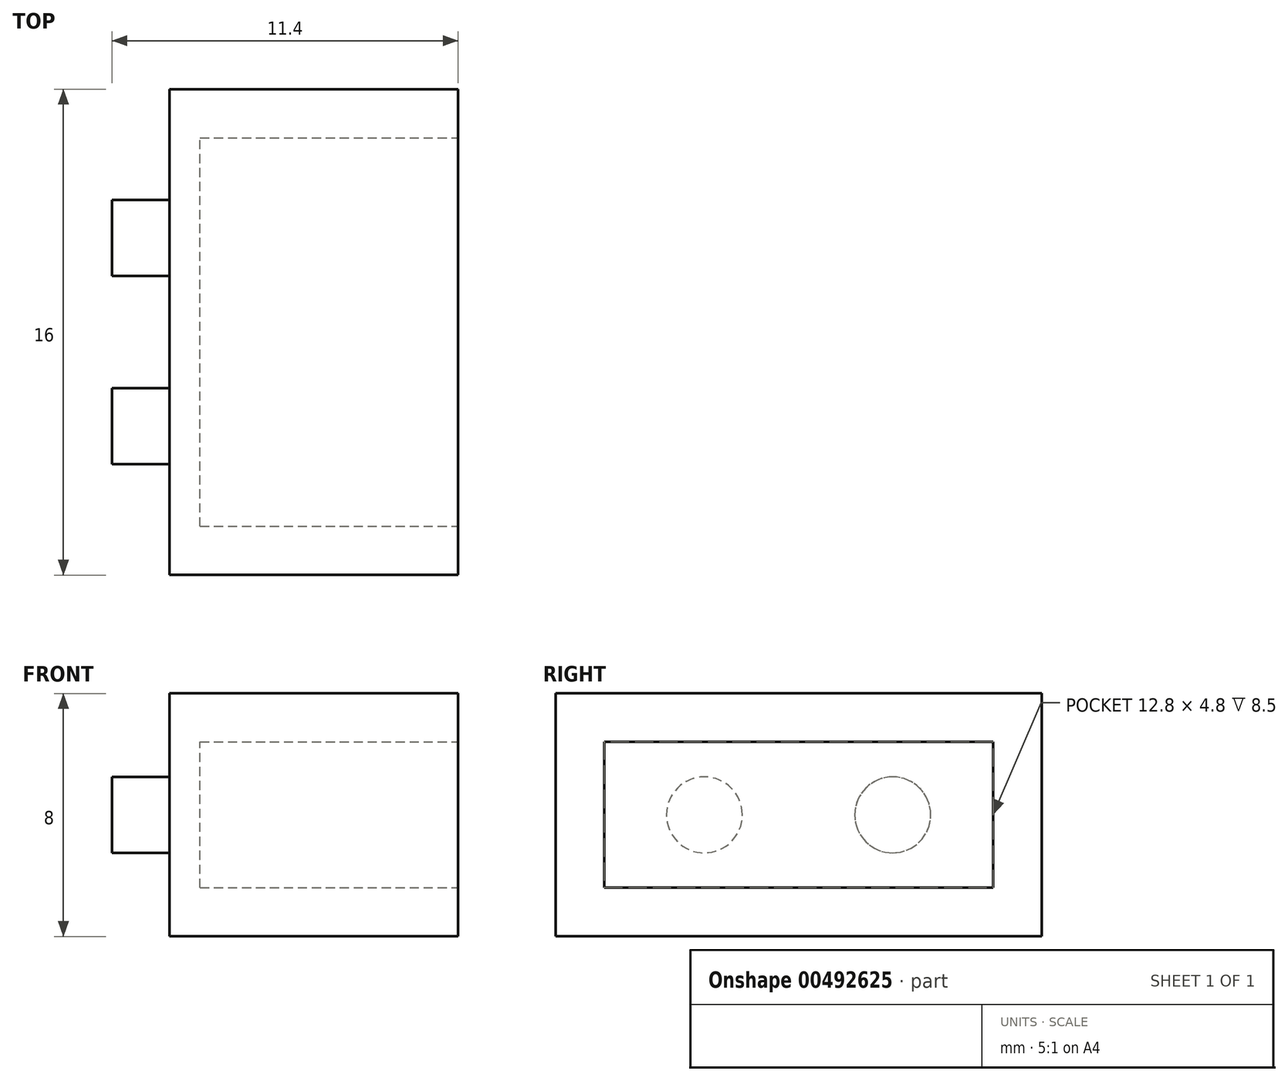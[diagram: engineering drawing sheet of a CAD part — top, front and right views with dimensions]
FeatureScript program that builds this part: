
annotation { "Feature Type Name" : "Feature", "Feature Type Description" : "" }
export const myFeature = defineFeature(function(context is Context, id is Id, definition is map)
    precondition{}
    {
        {
            var Q0;
            Q0=qCreatedBy(makeId("Right.planeOp"),FACE);
            var sketch = newSketch(context, id + "F0", { "sketchPlane" : qUnion([Q0])});
            skLineSegment(sketch, "E0.bottom", {"start": v(49.78, 25.94) * mm, "end": v(33.78, 25.94) * mm});
            skLineSegment(sketch, "E0.top", {"start": v(49.78, 17.94) * mm, "end": v(33.78, 17.94) * mm});
            skLineSegment(sketch, "E0.left", {"start": v(49.78, 25.94) * mm, "end": v(49.78, 17.94) * mm});
            skLineSegment(sketch, "E0.right", {"start": v(33.78, 25.94) * mm, "end": v(33.78, 17.94) * mm});
            skSolve(sketch);
        }
        {
            var Q0;
            Q0=makeQuery(id+"F0.imprint","IMPRINT",FACE,{"disambiguationData":[TD([[makeQuery(id+"F0.imprint","IMPRINT",EDGE,{"derivedFrom":sQuery(id+"F0.wireOp",EDGE,"E0.bottom")}),1.0]])]});
            extrude(context, id + "F1", {"entities" : qUnion([Q0]), "depth" : 9.5 * mm});
        }
        {
            var Q0;
            Q0=makeQuery(id+"F1.opExtrude","CAP_FACE",FACE,{"disambiguationData":[OSD([sQuery(id+"F0.wireOp",EDGE,"E0.bottom"),sQuery(id+"F0.wireOp",EDGE,"E0.top"),sQuery(id+"F0.wireOp",EDGE,"E0.left"),sQuery(id+"F0.wireOp",EDGE,"E0.right")])],"isStart":true});
            var sketch = newSketch(context, id + "F2", { "sketchPlane" : qUnion([Q0])});
            skCircle(sketch, "E1", {"center": v(-38.68, 21.94) * mm, "radius": 1.25 * mm});
            skCircle(sketch, "E2", {"center": v(-44.88, 21.94) * mm, "radius": 1.25 * mm});
            skSolve(sketch);
        }
        {
            var Q0;
            Q0=makeQuery(id+"F2.imprint","IMPRINT",FACE,{"disambiguationData":[TD([[makeQuery(id+"F2.imprint","IMPRINT",EDGE,{"derivedFrom":sQuery(id+"F2.wireOp",EDGE,"E2")}),1.0]])]});
            var Q1;
            Q1=makeQuery(id+"F2.imprint","IMPRINT",FACE,{"disambiguationData":[TD([[makeQuery(id+"F2.imprint","IMPRINT",EDGE,{"derivedFrom":sQuery(id+"F2.wireOp",EDGE,"E1")}),1.0]])]});
            var Q2;
            Q2=qSketchRegion(id+"F4",true);
            extrude(context, id + "F3", {"entities" : qUnion([Q0, Q1, Q2]), "operationType" : NewBodyOperationType.ADD, "depth" : 1.9 * mm});
        }
        {
            var Q0;
            Q0=makeQuery(id+"F1.opExtrude","CAP_FACE",FACE,{"disambiguationData":[OSD([sQuery(id+"F0.wireOp",EDGE,"E0.bottom"),sQuery(id+"F0.wireOp",EDGE,"E0.top"),sQuery(id+"F0.wireOp",EDGE,"E0.left"),sQuery(id+"F0.wireOp",EDGE,"E0.right")])],"isStart":false});
            var sketch = newSketch(context, id + "F4", { "sketchPlane" : qUnion([Q0])});
            skLineSegment(sketch, "E3", {"start": v(48.18, 19.54) * mm, "end": v(48.18, 24.34) * mm});
            skLineSegment(sketch, "E4", {"start": v(48.18, 24.34) * mm, "end": v(35.38, 24.34) * mm});
            skLineSegment(sketch, "E5", {"start": v(35.38, 24.34) * mm, "end": v(35.38, 19.54) * mm});
            skLineSegment(sketch, "E6", {"start": v(35.38, 19.54) * mm, "end": v(48.18, 19.54) * mm});
            skSolve(sketch);
        }
        {
            var Q0;
            Q0=qCreatedBy(makeId("Right.planeOp"),FACE);
            var sketch = newSketch(context, id + "F5", { "sketchPlane" : qUnion([Q0])});
            skSolve(sketch);
        }
        {
            var Q0;
            Q0=qSketchRegion(id+"F5",true);
            var Q1;
            Q1=makeQuery(id+"F4.imprint","IMPRINT",FACE,{"disambiguationData":[TD([[makeQuery(id+"F4.imprint","IMPRINT",EDGE,{"derivedFrom":sQuery(id+"F4.wireOp",EDGE,"E3")}),1.0]])]});
            extrude(context, id + "F6", {"entities" : qUnion([Q0, Q1]), "operationType" : NewBodyOperationType.REMOVE, "oppositeDirection" : true, "depth" : 8.5 * mm});
        }
    });
